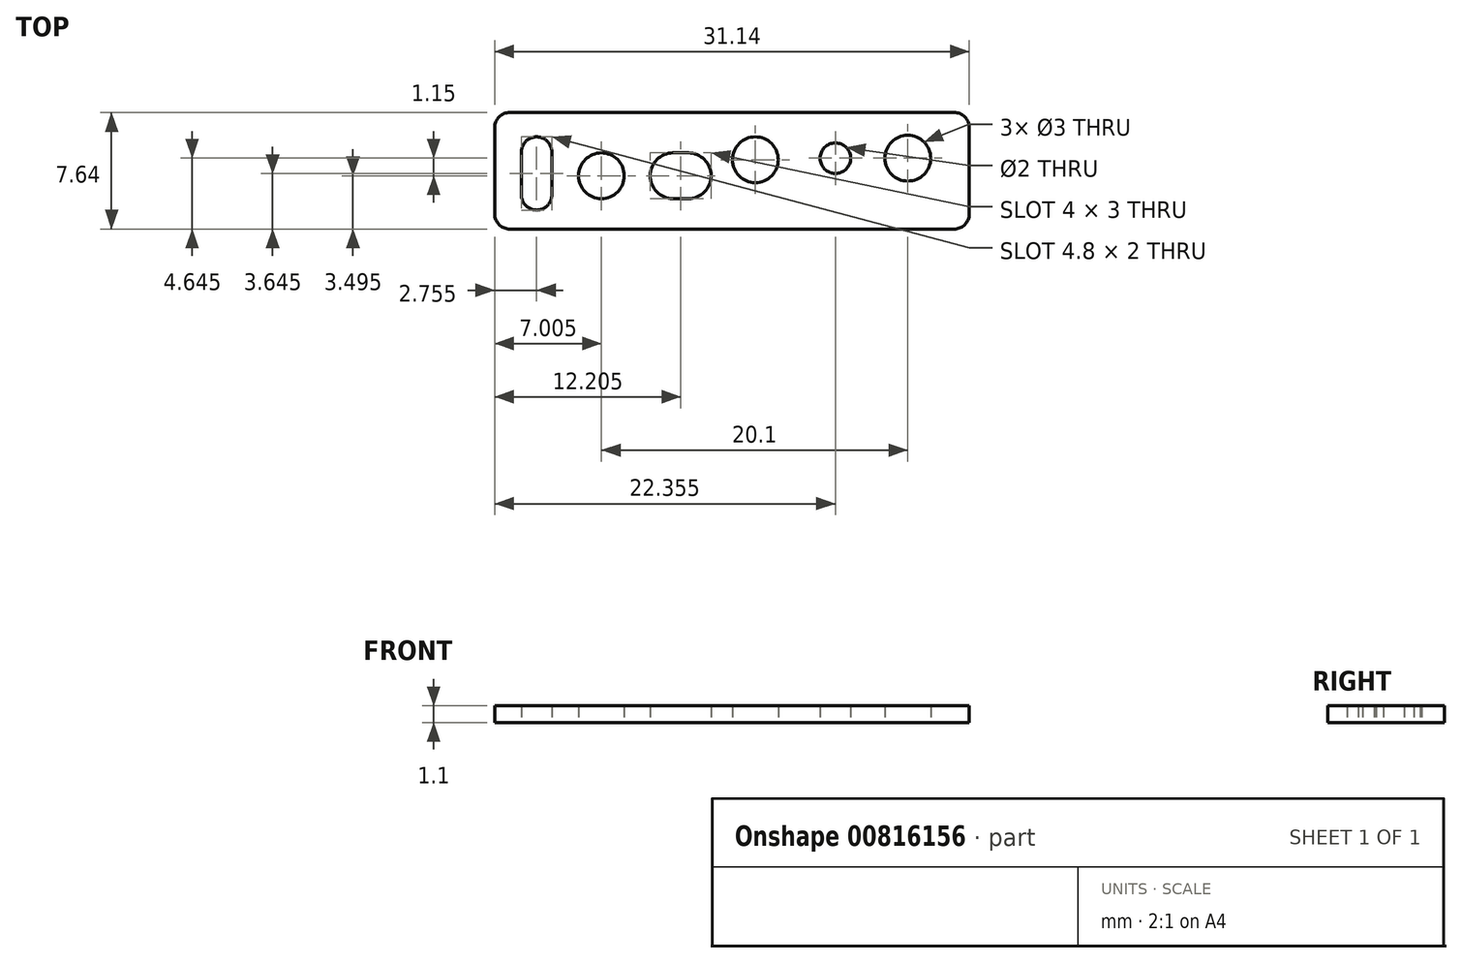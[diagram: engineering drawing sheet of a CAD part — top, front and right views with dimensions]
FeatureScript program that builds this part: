
annotation { "Feature Type Name" : "Feature", "Feature Type Description" : "" }
export const myFeature = defineFeature(function(context is Context, id is Id, definition is map)
    precondition{}
    {
        {
            var Q0;
            Q0=qCreatedBy(makeId("Top.planeOp"),FACE);
            var sketch = newSketch(context, id + "F0", { "sketchPlane" : qUnion([Q0])});
            skLineSegment(sketch, "E0.bottom", {"start": v(15.57, -3.82) * mm, "end": v(-15.56, -3.82) * mm});
            skLineSegment(sketch, "E0.top", {"start": v(15.57, 3.83) * mm, "end": v(-15.56, 3.83) * mm});
            skLineSegment(sketch, "E0.left", {"start": v(15.57, -3.82) * mm, "end": v(15.57, 3.83) * mm});
            skLineSegment(sketch, "E0.right", {"start": v(-15.56, -3.82) * mm, "end": v(-15.56, 3.83) * mm});
            skPoint(sketch, "E0.middle", {"position": v(0, 0) * mm});
            skCircle(sketch, "E1", {"center": v(-8.56, -0.32) * mm, "radius": 1.5 * mm});
            skCircle(sketch, "E2", {"center": v(1.54, 0.73) * mm, "radius": 1.5 * mm});
            skCircle(sketch, "E3", {"center": v(11.54, 0.83) * mm, "radius": 1.5 * mm});
            skArc(sketch, "E4", {"start": v(-13.81, -1.57) * mm, "mid": v(-12.8, -2.57) * mm, "end": v(-11.82, -1.55) * mm});
            skArc(sketch, "E5", {"start": v(-11.82, 1.22) * mm, "mid": v(-12.83, 2.22) * mm, "end": v(-13.81, 1.19) * mm});
            skLineSegment(sketch, "E6", {"start": v(-13.81, 1.26) * mm, "end": v(-13.81, -1.57) * mm});
            skLineSegment(sketch, "E7", {"start": v(-11.82, -1.6) * mm, "end": v(-11.82, 1.22) * mm});
            skArc(sketch, "E8", {"start": v(-3.86, 1.18) * mm, "mid": v(-5.36, -0.32) * mm, "end": v(-3.87, -1.82) * mm});
            skArc(sketch, "E9", {"start": v(-2.87, -1.82) * mm, "mid": v(-1.36, -0.33) * mm, "end": v(-2.86, 1.18) * mm});
            skLineSegment(sketch, "E10", {"start": v(-3.87, 1.18) * mm, "end": v(-2.86, 1.18) * mm});
            skLineSegment(sketch, "E11", {"start": v(-3.87, -1.82) * mm, "end": v(-2.87, -1.82) * mm});
            skCircle(sketch, "E12", {"center": v(6.79, 0.83) * mm, "radius": 1 * mm});
            skSolve(sketch);
        }
        {
            var Q0;
            Q0=makeQuery(id+"F0.imprint","IMPRINT",FACE,{"disambiguationData":[TD([[makeQuery(id+"F0.imprint","IMPRINT",EDGE,{"derivedFrom":sQuery(id+"F0.wireOp",EDGE,"E0.bottom")}),-1.0]])]});
            extrude(context, id + "F1", {"entities" : qUnion([Q0]), "endBound" : BoundingType.SYMMETRIC, "depth" : 1.1 * mm, "offsetDistance" : 25 * mm});
        }
        {
            var Q0;
            Q0=makeQuery(id+"F1.opExtrude","SWEPT_EDGE",EDGE,{"disambiguationData":[OSD([sQuery(id+"F0.wireOp",EDGE,"E0.top"),sQuery(id+"F0.wireOp",EDGE,"E0.right")])]});
            var Q1;
            Q1=makeQuery(id+"F1.opExtrude","SWEPT_EDGE",EDGE,{"disambiguationData":[OSD([sQuery(id+"F0.wireOp",EDGE,"E0.top"),sQuery(id+"F0.wireOp",EDGE,"E0.left")])]});
            var Q2;
            Q2=makeQuery(id+"F1.opExtrude","SWEPT_EDGE",EDGE,{"disambiguationData":[OSD([sQuery(id+"F0.wireOp",EDGE,"E0.bottom"),sQuery(id+"F0.wireOp",EDGE,"E0.left")])]});
            var Q3;
            Q3=makeQuery(id+"F1.opExtrude","SWEPT_EDGE",EDGE,{"disambiguationData":[OSD([sQuery(id+"F0.wireOp",EDGE,"E0.bottom"),sQuery(id+"F0.wireOp",EDGE,"E0.right")])]});
            fillet(context, id + "F2", {"entities" : qUnion([Q0, Q1, Q2, Q3]), "radius" : 1 * mm, "tangentPropagation" : true, "allowEdgeOverflow" : false});
        }
    });
